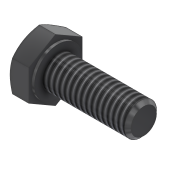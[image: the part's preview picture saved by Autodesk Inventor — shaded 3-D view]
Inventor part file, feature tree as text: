
AUTODESK INVENTOR PART (.ipt)
format: ipt  version: 2015 (Build 190159000, 159)  size: 221,696 bytes
history: native  units: mm
features: sketch x4, revolve x2, extrude x2, thread x1
ambient origin geometry x8: Origin, YZ Plane, XZ Plane, XY Plane, X Axis, Y Axis, Z Axis, Center Point
bodies: Solid1 (feature_tree)
feature tree (9):
  revolve  "Revolution1"  [1 undecoded]
  extrude  "Extrusion1"  Depth=8.9mm
  revolve  "Revolution2"  Angle=45.0deg
  thread  "Thread1"  [1 undecoded]
  extrude  "Extrusion2"  TaperAngle=90.0deg  [1 undecoded]
  sketch  "Sketch1"  dims[d0=6.0mm d1=16.0mm]
  sketch  "Sketch2"  dims[d2=10.0mm d3=8.9mm]
  sketch  "Sketch3"  dims[d4=4.0mm d5=45.0deg d6=4.77mm]
  sketch  "Sketch4"  dims[d7=0.5mm d8=90.0deg d9=10.0mm d10=0.0mm d11=11.1mm d12=1.11mm d13=30.0deg d14=90.0deg d15=10.0mm d16=0.0mm d17=7.5mm d18=0.1mm d19=0.0mm]
note: 3 required parameter values undecoded (feature->parameter linkage not recoverable at this tier; creation-order binding heuristic only, values carry confidence <= 0.55)